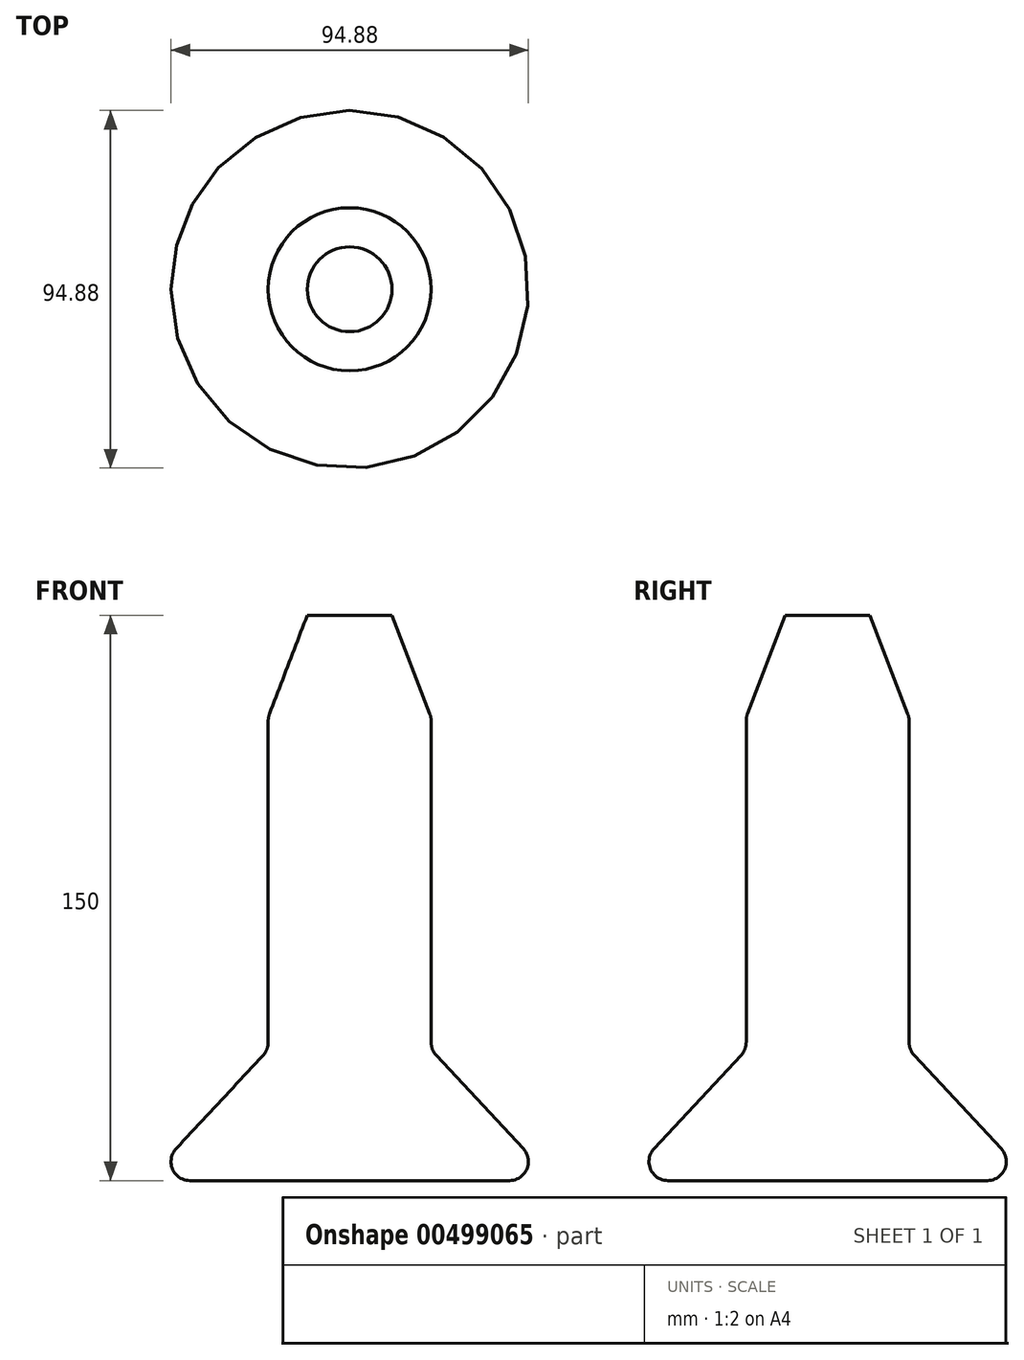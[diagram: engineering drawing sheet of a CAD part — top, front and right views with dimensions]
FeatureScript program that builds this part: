
annotation { "Feature Type Name" : "Feature", "Feature Type Description" : "" }
export const myFeature = defineFeature(function(context is Context, id is Id, definition is map)
    precondition{}
    {
        {
            var Q0;
            Q0=qCreatedBy(makeId("Front.planeOp"),FACE);
            var sketch = newSketch(context, id + "F0", { "sketchPlane" : qUnion([Q0])});
            skLineSegment(sketch, "E0", {"start": v(0, 0) * mm, "end": v(0, 150) * mm});
            skLineSegment(sketch, "E1", {"start": v(0, 0) * mm, "end": v(42.44, 0) * mm});
            skLineSegment(sketch, "E2", {"start": v(46.1, 8.4) * mm, "end": v(22.96, 33.27) * mm});
            skLineSegment(sketch, "E3", {"start": v(21.62, 36.68) * mm, "end": v(21.62, 121.95) * mm});
            skLineSegment(sketch, "E4", {"start": v(21.3, 123.74) * mm, "end": v(11.25, 150) * mm});
            skLineSegment(sketch, "E5", {"start": v(11.25, 150) * mm, "end": v(0, 150) * mm});
            skPoint(sketch, "E6.visualSharp", {"position": v(21.62, 122.87) * mm});
            skArc(sketch, "E6.filletArc", {"start": v(21.62, 121.95) * mm, "mid": v(21.54, 122.86) * mm, "end": v(21.3, 123.74) * mm});
            skPoint(sketch, "E7.visualSharp", {"position": v(21.62, 34.71) * mm});
            skArc(sketch, "E7.filletArc", {"start": v(21.62, 36.68) * mm, "mid": v(21.97, 34.85) * mm, "end": v(22.96, 33.27) * mm});
            skPoint(sketch, "E8.visualSharp", {"position": v(53.93, 0) * mm});
            skArc(sketch, "E8.filletArc", {"start": v(42.44, 0) * mm, "mid": v(47.03, 3) * mm, "end": v(46.1, 8.4) * mm});
            skSolve(sketch);
        }
        {
            var Q0;
            Q0 = qSketchRegion(id + "F0", true);
            var Q1;
            Q1=sQuery(id+"F0.wireOp",EDGE,"E0");
            revolve(context, id + "F1", {"surfaceOperationType" : NewSurfaceOperationType.NEW, "entities" : qUnion([Q0]), "axis" : qUnion([Q1]), "revolveType" : RevolveType.FULL});
        }
    });
